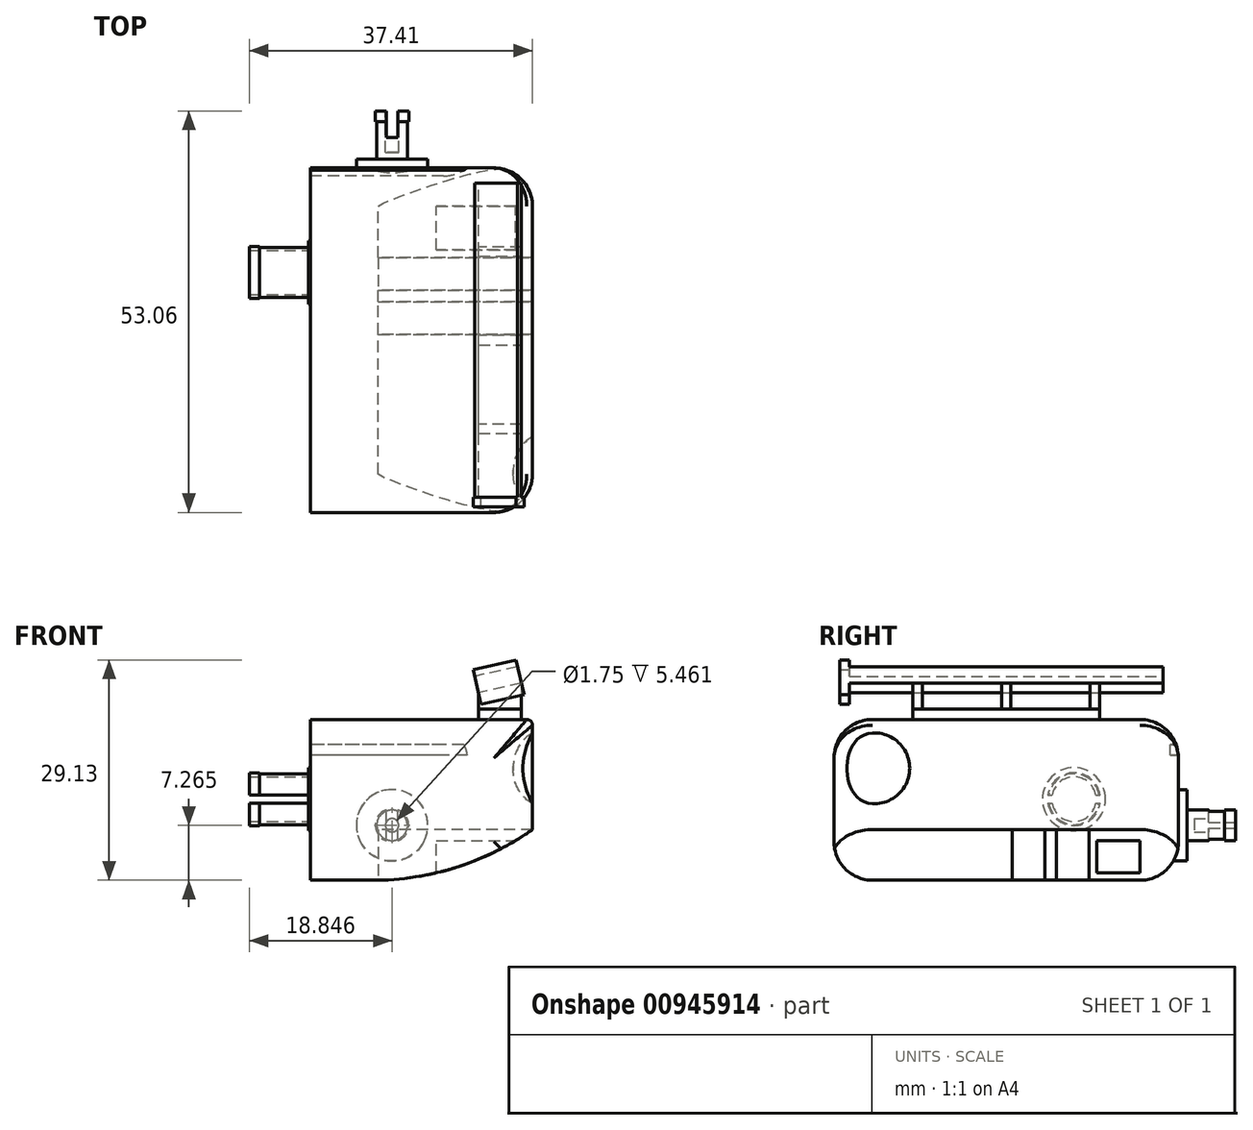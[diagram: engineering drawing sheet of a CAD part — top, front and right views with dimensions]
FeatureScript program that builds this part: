
annotation { "Feature Type Name" : "Feature", "Feature Type Description" : "" }
export const myFeature = defineFeature(function(context is Context, id is Id, definition is map)
    precondition{}
    {
        {
            var Q0;
            Q0=qCreatedBy(makeId("Front.planeOp"),FACE);
            var sketch = newSketch(context, id + "F0", { "sketchPlane" : qUnion([Q0])});
            skLineSegment(sketch, "E0.bottom", {"start": v(14.7, -10.63) * mm, "end": v(-14.7, -10.63) * mm});
            skLineSegment(sketch, "E0.top", {"start": v(14.7, 10.63) * mm, "end": v(-14.7, 10.63) * mm});
            skLineSegment(sketch, "E0.left", {"start": v(14.7, -10.63) * mm, "end": v(14.7, 10.63) * mm});
            skLineSegment(sketch, "E0.right", {"start": v(-14.7, -10.63) * mm, "end": v(-14.7, 10.63) * mm});
            skPoint(sketch, "E0.middle", {"position": v(0, 0) * mm});
            skSolve(sketch);
        }
        {
            var Q0;
            Q0=makeQuery(id+"F0.imprint","IMPRINT",FACE,{"disambiguationData":[TD([[makeQuery(id+"F0.imprint","IMPRINT",EDGE,{"derivedFrom":sQuery(id+"F0.wireOp",EDGE,"E0.bottom")}),-1.0]])]});
            extrude(context, id + "F1", {"entities" : qUnion([Q0]), "depth" : 45.54 * mm, "offsetDistance" : 25.4 * mm});
        }
        {
            var Q0;
            Q0=makeQuery(id+"F1.opExtrude","CAP_FACE",FACE,{"disambiguationData":[OSD([sQuery(id+"F0.wireOp",EDGE,"E0.bottom"),sQuery(id+"F0.wireOp",EDGE,"E0.top"),sQuery(id+"F0.wireOp",EDGE,"E0.left"),sQuery(id+"F0.wireOp",EDGE,"E0.right")])],"isStart":true});
            var sketch = newSketch(context, id + "F2", { "sketchPlane" : qUnion([Q0])});
            skCircle(sketch, "E1", {"center": v(3.87, -3.37) * mm, "radius": 4.72 * mm});
            skSolve(sketch);
        }
        {
            var Q0;
            Q0=makeQuery(id+"F2.imprint","IMPRINT",FACE,{"disambiguationData":[TD([[makeQuery(id+"F2.imprint","IMPRINT",EDGE,{"derivedFrom":sQuery(id+"F2.wireOp",EDGE,"E1")}),1.0]])]});
            extrude(context, id + "F3", {"entities" : qUnion([Q0]), "operationType" : NewBodyOperationType.ADD, "depth" : 1.14 * mm, "offsetDistance" : 25.4 * mm});
        }
        {
            var Q0;
            Q0=makeQuery(id+"F3.opExtrude","CAP_FACE",FACE,{"disambiguationData":[OSD([sQuery(id+"F2.wireOp",EDGE,"E1")])],"isStart":false});
            var sketch = newSketch(context, id + "F4", { "sketchPlane" : qUnion([Q0])});
            skCircle(sketch, "E2", {"center": v(3.87, -3.37) * mm, "radius": 2.02 * mm});
            skSolve(sketch);
        }
        {
            var Q0;
            Q0=makeQuery(id+"F4.imprint","IMPRINT",FACE,{"disambiguationData":[TD([[makeQuery(id+"F4.imprint","IMPRINT",EDGE,{"derivedFrom":sQuery(id+"F4.wireOp",EDGE,"E2")}),1.0]])]});
            extrude(context, id + "F5", {"entities" : qUnion([Q0]), "operationType" : NewBodyOperationType.ADD, "depth" : 4.95 * mm, "offsetDistance" : 25.4 * mm});
        }
        {
            var Q0;
            Q0=makeQuery(id+"F5.opExtrude","CAP_FACE",FACE,{"disambiguationData":[OSD([sQuery(id+"F4.wireOp",EDGE,"E2")])],"isStart":false});
            var sketch = newSketch(context, id + "F6", { "sketchPlane" : qUnion([Q0])});
            skCircle(sketch, "E3", {"center": v(3.87, -3.37) * mm, "radius": 2.2 * mm});
            skSolve(sketch);
        }
        {
            var Q0;
            Q0 = qSketchRegion(id + "F6", true);
            extrude(context, id + "F7", {"entities" : qUnion([Q0]), "operationType" : NewBodyOperationType.ADD, "depth" : 1.42 * mm, "offsetDistance" : 25.4 * mm});
        }
        {
            var Q0;
            Q0=makeQuery(id+"F7.opExtrude","CAP_FACE",FACE,{"disambiguationData":[OSD([sQuery(id+"F6.wireOp",EDGE,"E3")])],"isStart":false});
            var sketch = newSketch(context, id + "F8", { "sketchPlane" : qUnion([Q0])});
            skLineSegment(sketch, "E4.bottom", {"start": v(4.66, -5.93) * mm, "end": v(3.09, -5.93) * mm});
            skLineSegment(sketch, "E4.top", {"start": v(4.66, -0.8) * mm, "end": v(3.09, -0.8) * mm});
            skLineSegment(sketch, "E4.left", {"start": v(4.66, -5.93) * mm, "end": v(4.66, -0.8) * mm});
            skLineSegment(sketch, "E4.right", {"start": v(3.09, -5.93) * mm, "end": v(3.09, -0.8) * mm});
            skPoint(sketch, "E4.middle", {"position": v(3.87, -3.37) * mm});
            skSolve(sketch);
        }
        {
            var Q0;
            {var subQ0=sQuery(id+"F8.wireOp",EDGE,"E4.left");var subQ1=makeQuery(id+"F7.opExtrude","CAP_EDGE",EDGE,{"disambiguationData":[OSD([sQuery(id+"F6.wireOp",EDGE,"E3")])],"isStart":false});var subQ2=makeQuery(id+"F8.imprint","INTERSECT",VERTEX,{"disambiguationData":[OD(0.0)],"derivedFrom":[subQ1,subQ0]});Q0=makeQuery(id+"F8.imprint","IMPRINT",FACE,{"disambiguationData":[TD([[makeQuery(id+"F8.imprint","IMPRINT",EDGE,{"disambiguationData":[TD([[subQ2,-1.0]])],"derivedFrom":subQ0}),1.0]])]});}
            extrude(context, id + "F9", {"entities" : qUnion([Q0]), "operationType" : NewBodyOperationType.REMOVE, "oppositeDirection" : true, "depth" : 3.5 * mm, "offsetDistance" : 25.4 * mm});
        }
        {
            var Q0;
            {var subQ0=sQuery(id+"F6.wireOp",EDGE,"E3");Q0=makeQuery(id+"F9.boolean.opBoolean","SPLIT",FACE,{"disambiguationData":[TD([makeQuery(id+"F9.opExtrude","SWEPT_FACE",FACE,{"disambiguationData":[OSD([sQuery(id+"F8.wireOp",EDGE,"E4.right")])]})])],"derivedFrom":makeQuery(id+"F7.opExtrude","CAP_FACE",FACE,{"disambiguationData":[OSD([subQ0])],"isStart":false})});}
            var sketch = newSketch(context, id + "F10", { "sketchPlane" : qUnion([Q0])});
            skCircle(sketch, "E5", {"center": v(3.87, -3.37) * mm, "radius": 0.88 * mm});
            skSolve(sketch);
        }
        {
            var Q0;
            {var subQ0=sQuery(id+"F10.wireOp",EDGE,"E5");var subQ1=makeQuery(id+"F9.boolean.opBoolean","COPY",EDGE,{"derivedFrom":makeQuery(id+"F9.opExtrude","CAP_EDGE",EDGE,{"disambiguationData":[OSD([sQuery(id+"F8.wireOp",EDGE,"E4.right")])],"isStart":true})});var subQ2=makeQuery(id+"F10.imprint","INTERSECT",VERTEX,{"disambiguationData":[OD(0.0)],"derivedFrom":[subQ1,subQ0]});Q0=makeQuery(id+"F10.imprint","IMPRINT",FACE,{"disambiguationData":[TD([[makeQuery(id+"F10.imprint","IMPRINT",EDGE,{"disambiguationData":[TD([[subQ2,1.0]])],"derivedFrom":subQ0}),1.0]])]});}
            var Q1;
            {var subQ0=sQuery(id+"F10.wireOp",EDGE,"E5");var subQ1=makeQuery(id+"F9.boolean.opBoolean","COPY",EDGE,{"derivedFrom":makeQuery(id+"F9.opExtrude","CAP_EDGE",EDGE,{"disambiguationData":[OSD([sQuery(id+"F8.wireOp",EDGE,"E4.right")])],"isStart":true})});var subQ2=makeQuery(id+"F10.imprint","INTERSECT",VERTEX,{"disambiguationData":[OD(0.0)],"derivedFrom":[subQ1,subQ0]});Q1=makeQuery(id+"F10.imprint","IMPRINT",FACE,{"disambiguationData":[TD([[makeQuery(id+"F10.imprint","IMPRINT",EDGE,{"disambiguationData":[TD([[subQ2,-1.0]])],"derivedFrom":subQ0}),1.0]])]});}
            extrude(context, id + "F11", {"entities" : qUnion([Q0, Q1]), "operationType" : NewBodyOperationType.REMOVE, "oppositeDirection" : true, "depth" : 5.46 * mm, "offsetDistance" : 25.4 * mm});
        }
        {
            var Q0;
            Q0=makeQuery(id+"F1.opExtrude","CAP_FACE",FACE,{"disambiguationData":[OSD([sQuery(id+"F0.wireOp",EDGE,"E0.bottom"),sQuery(id+"F0.wireOp",EDGE,"E0.top"),sQuery(id+"F0.wireOp",EDGE,"E0.left"),sQuery(id+"F0.wireOp",EDGE,"E0.right")])],"isStart":false});
            var sketch = newSketch(context, id + "F12", { "sketchPlane" : qUnion([Q0])});
            skSolve(sketch);
        }
        {
            var Q0;
            Q0=makeQuery(id+"F12.imprint","IMPRINT",FACE,{"disambiguationData":[TD([[makeQuery(id+"F12.imprint","IMPRINT",EDGE,{"derivedFrom":makeQuery(id+"F1.opExtrude","CAP_EDGE",EDGE,{"disambiguationData":[OSD([sQuery(id+"F0.wireOp",EDGE,"E0.bottom")])],"isStart":false})}),-1.0]])]});
            var Q1;
            Q1=makeQuery(id+"F1.opExtrude","CAP_FACE",FACE,{"disambiguationData":[OSD([sQuery(id+"F0.wireOp",EDGE,"E0.bottom"),sQuery(id+"F0.wireOp",EDGE,"E0.top"),sQuery(id+"F0.wireOp",EDGE,"E0.left"),sQuery(id+"F0.wireOp",EDGE,"E0.right")])],"isStart":true});
            cPlane(context, id + "F13", {"entities" : qUnion([Q0, Q1]), "cplaneType" : CPlaneType.MID_PLANE, "offset" : 25.4 * mm, "width" : 152.4 * mm, "height" : 152.4 * mm});
        }
        {
            var Q0;
            Q0=makeQuery(id+"F1.opExtrude","SWEPT_FACE",FACE,{"disambiguationData":[OSD([sQuery(id+"F0.wireOp",EDGE,"E0.right")])]});
            var sketch = newSketch(context, id + "F14", { "sketchPlane" : qUnion([Q0])});
            skCircle(sketch, "E6", {"center": v(13.82, 0.09) * mm, "radius": 4.17 * mm});
            skSolve(sketch);
        }
        {
            var Q0;
            Q0=makeQuery(id+"F14.imprint","IMPRINT",FACE,{"disambiguationData":[TD([[makeQuery(id+"F14.imprint","IMPRINT",EDGE,{"derivedFrom":sQuery(id+"F14.wireOp",EDGE,"E6")}),1.0]])]});
            extrude(context, id + "F15", {"entities" : qUnion([Q0]), "operationType" : NewBodyOperationType.ADD, "depth" : 0.25 * mm, "offsetDistance" : 25.4 * mm});
        }
        {
            var Q0;
            Q0=makeQuery(id+"F15.opExtrude","CAP_FACE",FACE,{"disambiguationData":[OSD([sQuery(id+"F14.wireOp",EDGE,"E6")])],"isStart":false});
            var sketch = newSketch(context, id + "F16", { "sketchPlane" : qUnion([Q0])});
            skCircle(sketch, "E7", {"center": v(13.82, 0.09) * mm, "radius": 3.37 * mm});
            skSolve(sketch);
        }
        {
            var Q0;
            Q0=makeQuery(id+"F16.imprint","IMPRINT",FACE,{"disambiguationData":[TD([[makeQuery(id+"F16.imprint","IMPRINT",EDGE,{"derivedFrom":sQuery(id+"F16.wireOp",EDGE,"E7")}),1.0]])]});
            extrude(context, id + "F17", {"entities" : qUnion([Q0]), "operationType" : NewBodyOperationType.ADD, "depth" : 6.43 * mm, "offsetDistance" : 25.4 * mm});
        }
        {
            var Q0;
            Q0=makeQuery(id+"F17.opExtrude","CAP_FACE",FACE,{"disambiguationData":[OSD([sQuery(id+"F16.wireOp",EDGE,"E7")])],"isStart":false});
            var sketch = newSketch(context, id + "F18", { "sketchPlane" : qUnion([Q0])});
            skCircle(sketch, "E8", {"center": v(13.82, 0.09) * mm, "radius": 3.5 * mm});
            skSolve(sketch);
        }
        {
            var Q0;
            Q0 = qSketchRegion(id + "F18", true);
            extrude(context, id + "F19", {"entities" : qUnion([Q0]), "operationType" : NewBodyOperationType.ADD, "depth" : 1.35 * mm, "offsetDistance" : 25.4 * mm});
        }
        {
            var Q0;
            Q0=makeQuery(id+"F19.opExtrude","CAP_FACE",FACE,{"disambiguationData":[OSD([sQuery(id+"F18.wireOp",EDGE,"E8")])],"isStart":false});
            var sketch = newSketch(context, id + "F20", { "sketchPlane" : qUnion([Q0])});
            skLineSegment(sketch, "E9.bottom", {"start": v(17.37, -0.46) * mm, "end": v(10.26, -0.46) * mm});
            skLineSegment(sketch, "E9.top", {"start": v(17.37, 0.63) * mm, "end": v(10.26, 0.63) * mm});
            skLineSegment(sketch, "E9.left", {"start": v(17.37, -0.46) * mm, "end": v(17.37, 0.63) * mm});
            skLineSegment(sketch, "E9.right", {"start": v(10.26, -0.46) * mm, "end": v(10.26, 0.63) * mm});
            skPoint(sketch, "E9.middle", {"position": v(13.82, 0.09) * mm});
            skSolve(sketch);
        }
        {
            var Q0;
            {var subQ0=sQuery(id+"F20.wireOp",EDGE,"E9.bottom");var subQ1=makeQuery(id+"F19.opExtrude","CAP_EDGE",EDGE,{"disambiguationData":[OSD([sQuery(id+"F18.wireOp",EDGE,"E8")])],"isStart":false});var subQ2=makeQuery(id+"F20.imprint","INTERSECT",VERTEX,{"disambiguationData":[OD(0.0)],"derivedFrom":[subQ1,subQ0]});Q0=makeQuery(id+"F20.imprint","IMPRINT",FACE,{"disambiguationData":[TD([[makeQuery(id+"F20.imprint","IMPRINT",EDGE,{"disambiguationData":[TD([[subQ2,-1.0]])],"derivedFrom":subQ0}),-1.0]])]});}
            extrude(context, id + "F21", {"entities" : qUnion([Q0]), "operationType" : NewBodyOperationType.REMOVE, "oppositeDirection" : true, "depth" : 7.77 * mm, "offsetDistance" : 25.4 * mm});
        }
        {
            var Q0;
            Q0=makeQuery(id+"F21.boolean.opBoolean","MERGE",FACE,{"derivedFrom":[makeQuery(id+"F15.opExtrude","CAP_FACE",FACE,{"disambiguationData":[OSD([sQuery(id+"F14.wireOp",EDGE,"E6")])],"isStart":false})],"fromTools":[makeQuery(id+"F21.opExtrude","CAP_FACE",FACE,{"disambiguationData":[OSD([sQuery(id+"F18.wireOp",EDGE,"E8"),sQuery(id+"F20.wireOp",EDGE,"E9.bottom"),sQuery(id+"F20.wireOp",EDGE,"E9.top")])],"isStart":false})]});
            var sketch = newSketch(context, id + "F22", { "sketchPlane" : qUnion([Q0])});
            skPoint(sketch, "E10", {"position": v(13.82, 0.09) * mm});
            skSolve(sketch);
        }
        {
            var Q0;
            Q0=sQuery(id+"F22.wireOp",VERTEX,"E10");
            var Q1;
            Q1=makeQuery(id+"F1.opExtrude","SWEPT_BODY",BODY,{"disambiguationData":[OSD([sQuery(id+"F0.wireOp",EDGE,"E0.bottom"),sQuery(id+"F0.wireOp",EDGE,"E0.top"),sQuery(id+"F0.wireOp",EDGE,"E0.left"),sQuery(id+"F0.wireOp",EDGE,"E0.right")])]});
            hole(context, id + "F23", {"style" : HoleStyle.SIMPLE, "endStyle" : HoleEndStyle.THROUGH, "oppositeDirection" : true, "holeDiameter" : 5.9 * mm, "majorDiameter" : 6.35 * mm, "isTappedThrough" : true, "tappedDepth" : 12.7 * mm, "tapClearance" : 3, "locations" : qUnion([Q0]), "scope" : qUnion([Q1])});
        }
        {
            var Q0;
            Q0=makeQuery(id+"F1.opExtrude","SWEPT_FACE",FACE,{"disambiguationData":[OSD([sQuery(id+"F0.wireOp",EDGE,"E0.left")])]});
            var sketch = newSketch(context, id + "F24", { "sketchPlane" : qUnion([Q0])});
            skPoint(sketch, "E11", {"position": v(-40.22, 4.17) * mm});
            skCircle(sketch, "E12", {"center": v(-40.22, 4.17) * mm, "radius": 4.69 * mm});
            skSolve(sketch);
        }
        {
            var Q0;
            Q0=makeQuery(id+"F24.imprint","IMPRINT",FACE,{"disambiguationData":[TD([[makeQuery(id+"F24.imprint","IMPRINT",EDGE,{"derivedFrom":sQuery(id+"F24.wireOp",EDGE,"E12")}),1.0]])]});
            extrude(context, id + "F25", {"entities" : qUnion([Q0]), "operationType" : NewBodyOperationType.REMOVE, "oppositeDirection" : true, "depth" : 2.54 * mm, "offsetDistance" : 25.4 * mm});
        }
        {
            var Q0;
            Q0=makeQuery(id+"F25.boolean.opBoolean","COPY",FACE,{"derivedFrom":makeQuery(id+"F25.opExtrude","CAP_FACE",FACE,{"disambiguationData":[OSD([sQuery(id+"F24.wireOp",EDGE,"E12")])],"isStart":false})});
            fillet(context, id + "F26", {"entities" : qUnion([Q0]), "radius" : 5.08 * mm, "tangentPropagation" : true, "allowEdgeOverflow" : false});
        }
        {
            var Q0;
            Q0=makeQuery(id+"F1.opExtrude","CAP_FACE",FACE,{"disambiguationData":[OSD([sQuery(id+"F0.wireOp",EDGE,"E0.bottom"),sQuery(id+"F0.wireOp",EDGE,"E0.top"),sQuery(id+"F0.wireOp",EDGE,"E0.left"),sQuery(id+"F0.wireOp",EDGE,"E0.right")])],"isStart":true});
            var sketch = newSketch(context, id + "F27", { "sketchPlane" : qUnion([Q0])});
            skLineSegment(sketch, "E13.bottom", {"start": v(-6.03, 7.28) * mm, "end": v(14.7, 7.28) * mm});
            skLineSegment(sketch, "E13.top", {"start": v(-6.03, 5.93) * mm, "end": v(14.7, 5.93) * mm});
            skLineSegment(sketch, "E13.left", {"start": v(-6.03, 7.28) * mm, "end": v(-6.03, 5.93) * mm});
            skLineSegment(sketch, "E13.right", {"start": v(14.7, 7.28) * mm, "end": v(14.7, 5.93) * mm});
            skSolve(sketch);
        }
        {
            var Q0;
            Q0 = qSketchRegion(id + "F27", true);
            extrude(context, id + "F28", {"entities" : qUnion([Q0]), "operationType" : NewBodyOperationType.REMOVE, "oppositeDirection" : true, "depth" : 1.07 * mm, "offsetDistance" : 25.4 * mm});
        }
        {
            var Q0;
            Q0=makeQuery(id+"F28.boolean.opBoolean","COPY",EDGE,{"derivedFrom":makeQuery(id+"F28.opExtrude","CAP_EDGE",EDGE,{"disambiguationData":[OSD([sQuery(id+"F27.wireOp",EDGE,"E13.left")])],"isStart":false})});
            fillet(context, id + "F29", {"entities" : qUnion([Q0]), "radius" : 5.08 * mm, "tangentPropagation" : true, "allowEdgeOverflow" : false});
        }
        {
            var Q0;
            Q0=makeQuery(id+"F1.opExtrude","CAP_VERTEX",VERTEX,{"disambiguationData":[OSD([sQuery(id+"F0.wireOp",EDGE,"E0.top"),sQuery(id+"F0.wireOp",EDGE,"E0.left")])],"isStart":true});
            var Q1;
            Q1=makeQuery(id+"F1.opExtrude","CAP_VERTEX",VERTEX,{"disambiguationData":[OSD([sQuery(id+"F0.wireOp",EDGE,"E0.top"),sQuery(id+"F0.wireOp",EDGE,"E0.right")])],"isStart":true});
            var Q2;
            Q2=makeQuery(id+"F1.opExtrude","CAP_VERTEX",VERTEX,{"disambiguationData":[OSD([sQuery(id+"F0.wireOp",EDGE,"E0.top"),sQuery(id+"F0.wireOp",EDGE,"E0.left")])],"isStart":false});
            cPlane(context, id + "F30", {"entities" : qUnion([Q0, Q1, Q2]), "cplaneType" : CPlaneType.THREE_POINT, "offset" : 25.4 * mm, "width" : 152.4 * mm, "height" : 152.4 * mm});
        }
        {
            var Q0;
            Q0=qCreatedBy(id+"F30.planeOp",FACE);
            var sketch = newSketch(context, id + "F31", { "sketchPlane" : qUnion([Q0])});
            skLineSegment(sketch, "E14.bottom", {"start": v(13.22, 35.1) * mm, "end": v(7.56, 35.1) * mm});
            skLineSegment(sketch, "E14.top", {"start": v(13.22, 10.44) * mm, "end": v(7.56, 10.44) * mm});
            skLineSegment(sketch, "E14.left", {"start": v(13.22, 35.1) * mm, "end": v(13.22, 10.44) * mm});
            skLineSegment(sketch, "E14.right", {"start": v(7.56, 35.1) * mm, "end": v(7.56, 10.44) * mm});
            skPoint(sketch, "E14.middle", {"position": v(10.39, 22.77) * mm});
            skSolve(sketch);
        }
        {
            var Q0;
            Q0=makeQuery(id+"F31.imprint","IMPRINT",FACE,{"disambiguationData":[TD([[makeQuery(id+"F31.imprint","IMPRINT",EDGE,{"derivedFrom":sQuery(id+"F31.wireOp",EDGE,"E14.bottom")}),1.0]])]});
            extrude(context, id + "F32", {"entities" : qUnion([Q0]), "operationType" : NewBodyOperationType.ADD, "oppositeDirection" : true, "depth" : 1.37 * mm, "offsetDistance" : 25.4 * mm});
        }
        {
            var Q0;
            Q0=makeQuery(id+"F32.opExtrude","CAP_FACE",FACE,{"disambiguationData":[OSD([sQuery(id+"F31.wireOp",EDGE,"E14.bottom"),sQuery(id+"F31.wireOp",EDGE,"E14.top"),sQuery(id+"F31.wireOp",EDGE,"E14.left"),sQuery(id+"F31.wireOp",EDGE,"E14.right")])],"isStart":false});
            var sketch = newSketch(context, id + "F33", { "sketchPlane" : qUnion([Q0])});
            skSolve(sketch);
        }
        {
            var Q0;
            Q0=makeQuery(id+"F33.imprint","IMPRINT",FACE,{"disambiguationData":[TD([[makeQuery(id+"F33.imprint","IMPRINT",EDGE,{"derivedFrom":makeQuery(id+"F32.opExtrude","CAP_EDGE",EDGE,{"disambiguationData":[OSD([sQuery(id+"F31.wireOp",EDGE,"E14.bottom")])],"isStart":false})}),-1.0]])]});
            var sketch = newSketch(context, id + "F34", { "sketchPlane" : qUnion([Q0])});
            skLineSegment(sketch, "E15.bottom", {"start": v(7.56, -10.44) * mm, "end": v(13.22, -10.44) * mm});
            skLineSegment(sketch, "E15.top", {"start": v(7.56, -11.68) * mm, "end": v(13.22, -11.68) * mm});
            skLineSegment(sketch, "E15.left", {"start": v(7.56, -10.44) * mm, "end": v(7.56, -11.68) * mm});
            skLineSegment(sketch, "E15.right", {"start": v(13.22, -10.44) * mm, "end": v(13.22, -11.68) * mm});
            skLineSegment(sketch, "E16.bottom", {"start": v(7.56, -22.15) * mm, "end": v(13.22, -22.15) * mm});
            skLineSegment(sketch, "E16.top", {"start": v(7.56, -23.4) * mm, "end": v(13.22, -23.4) * mm});
            skLineSegment(sketch, "E16.left", {"start": v(7.56, -22.15) * mm, "end": v(7.56, -23.4) * mm});
            skLineSegment(sketch, "E16.right", {"start": v(13.22, -22.15) * mm, "end": v(13.22, -23.4) * mm});
            skLineSegment(sketch, "E17.bottom", {"start": v(7.56, -33.86) * mm, "end": v(13.22, -33.86) * mm});
            skLineSegment(sketch, "E17.top", {"start": v(7.56, -35.1) * mm, "end": v(13.22, -35.1) * mm});
            skLineSegment(sketch, "E17.left", {"start": v(7.56, -33.86) * mm, "end": v(7.56, -35.1) * mm});
            skLineSegment(sketch, "E17.right", {"start": v(13.22, -33.86) * mm, "end": v(13.22, -35.1) * mm});
            skLineSegment(sketch, "E18", {"start": v(10.39, -23.4) * mm, "end": v(10.39, -33.86) * mm});
            skLineSegment(sketch, "E19", {"start": v(10.39, -22.15) * mm, "end": v(10.39, -11.68) * mm});
            skSolve(sketch);
        }
        {
            var Q0;
            Q0 = qSketchRegion(id + "F34", true);
            extrude(context, id + "F35", {"entities" : qUnion([Q0]), "depth" : 3.4 * mm, "offsetDistance" : 25.4 * mm});
        }
        {
            var Q0;
            Q0=makeQuery(id+"F35.opExtrude","CAP_EDGE",EDGE,{"disambiguationData":[OSD([sQuery(id+"F34.wireOp",EDGE,"E15.left")])],"isStart":false});
            var Q1;
            Q1=makeQuery(id+"F35.opExtrude","CAP_EDGE",EDGE,{"disambiguationData":[OSD([sQuery(id+"F34.wireOp",EDGE,"E16.left")])],"isStart":false});
            var Q2;
            Q2=makeQuery(id+"F35.opExtrude","CAP_EDGE",EDGE,{"disambiguationData":[OSD([sQuery(id+"F34.wireOp",EDGE,"E17.left")])],"isStart":false});
            chamfer(context, id + "F36", {"entities" : qUnion([Q0, Q1, Q2]), "chamferType" : ChamferType.OFFSET_ANGLE, "width" : 1.27 * mm, "oppositeDirection" : false, "angle" : 77.36 * degree, "tangentPropagation" : true});
        }
        {
            var Q0;
            Q0=makeQuery(id+"F36.opChamfer","BLEND_VERTEX",VERTEX,{"blendedFrom":[makeQuery(id+"F35.opExtrude","CAP_EDGE",EDGE,{"disambiguationData":[OSD([sQuery(id+"F34.wireOp",EDGE,"E16.left")])],"isStart":false}),makeQuery(id+"F35.opExtrude","SWEPT_FACE",FACE,{"disambiguationData":[OSD([sQuery(id+"F34.wireOp",EDGE,"E16.bottom")])]}),makeQuery(id+"F35.opExtrude","SWEPT_FACE",FACE,{"disambiguationData":[OSD([sQuery(id+"F34.wireOp",EDGE,"E16.right")])]})],"blendedInto":[makeQuery(id+"F35.opExtrude","SWEPT_FACE",FACE,{"disambiguationData":[OSD([sQuery(id+"F34.wireOp",EDGE,"E16.bottom")])]}),makeQuery(id+"F35.opExtrude","SWEPT_FACE",FACE,{"disambiguationData":[OSD([sQuery(id+"F34.wireOp",EDGE,"E16.right")])]})]});
            var Q1;
            {var subQ0=sQuery(id+"F34.wireOp",EDGE,"E16.left");Q1=makeQuery(id+"F36.opChamfer","BLEND_VERTEX",VERTEX,{"blendedFrom":[makeQuery(id+"F35.opExtrude","CAP_EDGE",EDGE,{"disambiguationData":[OSD([subQ0])],"isStart":false}),makeQuery(id+"F35.opExtrude","SWEPT_FACE",FACE,{"disambiguationData":[OSD([sQuery(id+"F34.wireOp",EDGE,"E16.bottom")])]}),makeQuery(id+"F35.opExtrude","SWEPT_FACE",FACE,{"disambiguationData":[OSD([subQ0])]})],"blendedInto":[makeQuery(id+"F35.opExtrude","SWEPT_FACE",FACE,{"disambiguationData":[OSD([sQuery(id+"F34.wireOp",EDGE,"E16.bottom")])]}),makeQuery(id+"F35.opExtrude","SWEPT_FACE",FACE,{"disambiguationData":[OSD([subQ0])]})]});}
            var Q2;
            {var subQ0=sQuery(id+"F34.wireOp",EDGE,"E16.left");Q2=makeQuery(id+"F36.opChamfer","BLEND_VERTEX",VERTEX,{"blendedFrom":[makeQuery(id+"F35.opExtrude","CAP_EDGE",EDGE,{"disambiguationData":[OSD([subQ0])],"isStart":false}),makeQuery(id+"F35.opExtrude","SWEPT_FACE",FACE,{"disambiguationData":[OSD([sQuery(id+"F34.wireOp",EDGE,"E16.top")])]}),makeQuery(id+"F35.opExtrude","SWEPT_FACE",FACE,{"disambiguationData":[OSD([subQ0])]})],"blendedInto":[makeQuery(id+"F35.opExtrude","SWEPT_FACE",FACE,{"disambiguationData":[OSD([sQuery(id+"F34.wireOp",EDGE,"E16.top")])]}),makeQuery(id+"F35.opExtrude","SWEPT_FACE",FACE,{"disambiguationData":[OSD([subQ0])]})]});}
            cPlane(context, id + "F37", {"entities" : qUnion([Q0, Q1, Q2]), "cplaneType" : CPlaneType.THREE_POINT, "offset" : 25.4 * mm, "width" : 152.4 * mm, "height" : 152.4 * mm});
        }
        {
            var Q0;
            Q0=qCreatedBy(id+"F37.planeOp",FACE);
            var sketch = newSketch(context, id + "F38", { "sketchPlane" : qUnion([Q0])});
            skPoint(sketch, "E20", {"position": v(13.37, 23.4) * mm});
            skPoint(sketch, "E21", {"position": v(13.37, 22.15) * mm});
            skPoint(sketch, "E22", {"position": v(10.47, 22.77) * mm});
            skPoint(sketch, "E23", {"position": v(16.27, 22.77) * mm});
            skLineSegment(sketch, "E24", {"start": v(10.47, 22.77) * mm, "end": v(16.27, 22.77) * mm});
            skLineSegment(sketch, "E25", {"start": v(13.37, 22.15) * mm, "end": v(13.37, 23.4) * mm});
            skLineSegment(sketch, "E26.bottom", {"start": v(16.27, 43.51) * mm, "end": v(10.47, 43.51) * mm});
            skLineSegment(sketch, "E26.top", {"start": v(16.27, 2.03) * mm, "end": v(10.47, 2.03) * mm});
            skLineSegment(sketch, "E26.left", {"start": v(16.27, 43.51) * mm, "end": v(16.27, 2.03) * mm});
            skLineSegment(sketch, "E26.right", {"start": v(10.47, 43.51) * mm, "end": v(10.47, 2.03) * mm});
            skPoint(sketch, "E26.middle", {"position": v(13.37, 22.77) * mm});
            skSolve(sketch);
        }
        {
            var Q0;
            {var subQ0=sQuery(id+"F38.wireOp",EDGE,"E26.top");Q0=makeQuery(id+"F38.imprint","IMPRINT",FACE,{"disambiguationData":[TD([[makeQuery(id+"F38.imprint","IMPRINT",EDGE,{"derivedFrom":subQ0}),-1.0]])]});}
            var Q1;
            {var subQ3=sQuery(id+"F38.wireOp",EDGE,"E26.bottom");Q1=makeQuery(id+"F38.imprint","IMPRINT",FACE,{"disambiguationData":[TD([[makeQuery(id+"F38.imprint","IMPRINT",EDGE,{"derivedFrom":subQ3}),1.0]])]});}
            extrude(context, id + "F39", {"entities" : qUnion([Q0, Q1]), "oppositeDirection" : true, "depth" : 2.26 * mm, "offsetDistance" : 25.4 * mm});
        }
        {
            var Q0;
            Q0=makeQuery(id+"F39.opExtrude","SWEPT_FACE",FACE,{"disambiguationData":[OSD([sQuery(id+"F38.wireOp",EDGE,"E26.bottom")])]});
            var sketch = newSketch(context, id + "F40", { "sketchPlane" : qUnion([Q0])});
            skLineSegment(sketch, "E27", {"start": v(7.56, 14.14) * mm, "end": v(7.9, 12.62) * mm});
            skLineSegment(sketch, "E28", {"start": v(7.9, 12.62) * mm, "end": v(13.56, 13.9) * mm});
            skLineSegment(sketch, "E29", {"start": v(13.22, 15.4) * mm, "end": v(13.56, 13.9) * mm});
            skLineSegment(sketch, "E30", {"start": v(7.06, 16.34) * mm, "end": v(6.86, 17.23) * mm});
            skLineSegment(sketch, "E31", {"start": v(6.86, 17.23) * mm, "end": v(12.53, 18.5) * mm});
            skLineSegment(sketch, "E32", {"start": v(12.53, 18.5) * mm, "end": v(12.73, 17.61) * mm});
            skSolve(sketch);
        }
        {
            var Q0;
            Q0=makeQuery(id+"F40.imprint","IMPRINT",FACE,{"disambiguationData":[TD([[makeQuery(id+"F40.imprint","IMPRINT",EDGE,{"derivedFrom":sQuery(id+"F40.wireOp",EDGE,"E30")}),-1.0]])]});
            var Q1;
            {var subQ0=sQuery(id+"F38.wireOp",EDGE,"E26.bottom");Q1=makeQuery(id+"F40.imprint","IMPRINT",FACE,{"disambiguationData":[TD([[makeQuery(id+"F40.imprint","IMPRINT",EDGE,{"derivedFrom":makeQuery(id+"F39.opExtrude","CAP_EDGE",EDGE,{"disambiguationData":[OSD([subQ0])],"isStart":true})}),-1.0]])]});}
            var Q2;
            Q2=makeQuery(id+"F40.imprint","IMPRINT",FACE,{"disambiguationData":[TD([[makeQuery(id+"F40.imprint","IMPRINT",EDGE,{"derivedFrom":sQuery(id+"F40.wireOp",EDGE,"E27")}),1.0]])]});
            extrude(context, id + "F41", {"entities" : qUnion([Q0, Q1, Q2]), "operationType" : NewBodyOperationType.ADD, "depth" : 1.3 * mm, "offsetDistance" : 25.4 * mm});
        }
        {
            var Q0;
            Q0=makeQuery(id+"F1.opExtrude","CAP_FACE",FACE,{"disambiguationData":[OSD([sQuery(id+"F0.wireOp",EDGE,"E0.bottom"),sQuery(id+"F0.wireOp",EDGE,"E0.top"),sQuery(id+"F0.wireOp",EDGE,"E0.left"),sQuery(id+"F0.wireOp",EDGE,"E0.right")])],"isStart":true});
            var sketch = newSketch(context, id + "F42", { "sketchPlane" : qUnion([Q0])});
            skArc(sketch, "E33", {"start": v(-14.7, -3.93) * mm, "mid": v(-5, -8.8) * mm, "end": v(5.69, -10.63) * mm});
            skLineSegment(sketch, "E34", {"start": v(-14.7, -10.63) * mm, "end": v(-14.7, -3.93) * mm});
            skSolve(sketch);
        }
        {
            var Q0;
            Q0=makeQuery(id+"F1.opExtrude","SWEPT_EDGE",EDGE,{"disambiguationData":[OSD([sQuery(id+"F0.wireOp",EDGE,"E0.top"),sQuery(id+"F0.wireOp",EDGE,"E0.left")])]});
            fillet(context, id + "F43", {"entities" : qUnion([Q0]), "radius" : 0.76 * mm, "tangentPropagation" : true, "allowEdgeOverflow" : false});
        }
        {
            var Q0;
            Q0=makeQuery(id+"F1.opExtrude","CAP_EDGE",EDGE,{"disambiguationData":[OSD([sQuery(id+"F0.wireOp",EDGE,"E0.left")])],"isStart":false});
            var Q1;
            Q1=makeQuery(id+"F1.opExtrude","CAP_EDGE",EDGE,{"disambiguationData":[OSD([sQuery(id+"F0.wireOp",EDGE,"E0.left")])],"isStart":true});
            fillet(context, id + "F44", {"entities" : qUnion([Q0, Q1]), "radius" : 5.08 * mm, "tangentPropagation" : true, "allowEdgeOverflow" : false});
        }
        {
            var Q0;
            Q0=makeQuery(id+"F1.opExtrude","SWEPT_FACE",FACE,{"disambiguationData":[OSD([sQuery(id+"F0.wireOp",EDGE,"E0.left")])]});
            var sketch = newSketch(context, id + "F45", { "sketchPlane" : qUnion([Q0])});
            skLineSegment(sketch, "E35.bottom", {"start": v(-4.57, -10.63) * mm, "end": v(-10.83, -10.63) * mm});
            skLineSegment(sketch, "E35.top", {"start": v(-4.57, -5.4) * mm, "end": v(-10.83, -5.4) * mm});
            skLineSegment(sketch, "E35.left", {"start": v(-4.57, -10.63) * mm, "end": v(-4.57, -5.4) * mm});
            skLineSegment(sketch, "E35.right", {"start": v(-10.83, -10.63) * mm, "end": v(-10.83, -5.4) * mm});
            skSolve(sketch);
        }
        {
            var Q0;
            Q0=makeQuery(id+"F1.opExtrude","SWEPT_FACE",FACE,{"disambiguationData":[OSD([sQuery(id+"F0.wireOp",EDGE,"E0.bottom")])]});
            var sketch = newSketch(context, id + "F46", { "sketchPlane" : qUnion([Q0])});
            skPoint(sketch, "E36", {"position": v(14.7, 11.85) * mm});
            skLineSegment(sketch, "E37.bottom", {"start": v(14.7, 11.85) * mm, "end": v(-5.69, 11.85) * mm});
            skLineSegment(sketch, "E37.top", {"start": v(14.7, 16.17) * mm, "end": v(-5.69, 16.17) * mm});
            skLineSegment(sketch, "E37.left", {"start": v(14.7, 11.85) * mm, "end": v(14.7, 16.17) * mm});
            skLineSegment(sketch, "E37.right", {"start": v(-5.69, 11.85) * mm, "end": v(-5.69, 16.17) * mm});
            skLineSegment(sketch, "E38.bottom", {"start": v(14.7, 22) * mm, "end": v(-5.69, 22) * mm});
            skLineSegment(sketch, "E38.top", {"start": v(14.7, 17.7) * mm, "end": v(-5.69, 17.7) * mm});
            skLineSegment(sketch, "E38.left", {"start": v(14.7, 22) * mm, "end": v(14.7, 17.7) * mm});
            skLineSegment(sketch, "E38.right", {"start": v(-5.69, 22) * mm, "end": v(-5.69, 17.7) * mm});
            skLineSegment(sketch, "E39", {"start": v(14.7, 17.7) * mm, "end": v(14.7, 16.17) * mm});
            skLineSegment(sketch, "E40", {"start": v(14.7, 16.17) * mm, "end": v(14.7, 17.7) * mm});
            skLineSegment(sketch, "E41", {"start": v(14.7, 22.77) * mm, "end": v(14.7, 22) * mm});
            skSolve(sketch);
        }
        {
            var Q0;
            {var subQ0=sQuery(id+"F42.wireOp",EDGE,"E33");Q0=makeQuery(id+"F42.imprint","IMPRINT",FACE,{"disambiguationData":[TD([[makeQuery(id+"F42.imprint","IMPRINT",EDGE,{"derivedFrom":subQ0}),-1.0]])]});}
            extrude(context, id + "F47", {"entities" : qUnion([Q0]), "operationType" : NewBodyOperationType.REMOVE, "endBound" : BoundingType.THROUGH_ALL, "oppositeDirection" : true, "depth" : 25.4 * mm, "offsetDistance" : 25.4 * mm});
        }
        {
            var Q0;
            Q0=makeQuery(id+"F46.imprint","IMPRINT",FACE,{"disambiguationData":[TD([[makeQuery(id+"F46.imprint","IMPRINT",EDGE,{"derivedFrom":sQuery(id+"F46.wireOp",EDGE,"E37.bottom")}),-1.0]])]});
            var Q1;
            Q1=makeQuery(id+"F46.imprint","IMPRINT",FACE,{"disambiguationData":[TD([[makeQuery(id+"F46.imprint","IMPRINT",EDGE,{"derivedFrom":sQuery(id+"F46.wireOp",EDGE,"E38.bottom")}),1.0]])]});
            extrude(context, id + "F48", {"entities" : qUnion([Q0, Q1]), "operationType" : NewBodyOperationType.REMOVE, "oppositeDirection" : true, "depth" : 6.7 * mm, "offsetDistance" : 25.4 * mm});
        }
        {
            var Q0;
            Q0=makeQuery(id+"F45.imprint","IMPRINT",FACE,{"disambiguationData":[TD([[makeQuery(id+"F45.imprint","IMPRINT",EDGE,{"derivedFrom":sQuery(id+"F45.wireOp",EDGE,"E35.bottom")}),1.0]])]});
            extrude(context, id + "F49", {"entities" : qUnion([Q0]), "operationType" : NewBodyOperationType.REMOVE, "oppositeDirection" : true, "depth" : 12.7 * mm, "offsetDistance" : 25.4 * mm});
        }
        {
            var Q0;
            Q0=makeQuery(id+"F1.opExtrude","CAP_EDGE",EDGE,{"disambiguationData":[OSD([sQuery(id+"F0.wireOp",EDGE,"E0.bottom")])],"isStart":true});
            var Q1;
            Q1=makeQuery(id+"F1.opExtrude","CAP_EDGE",EDGE,{"disambiguationData":[OSD([sQuery(id+"F0.wireOp",EDGE,"E0.bottom")])],"isStart":false});
            fillet(context, id + "F50", {"entities" : qUnion([Q0, Q1]), "radius" : 5.08 * mm, "tangentPropagation" : true, "allowEdgeOverflow" : false});
        }
    });
